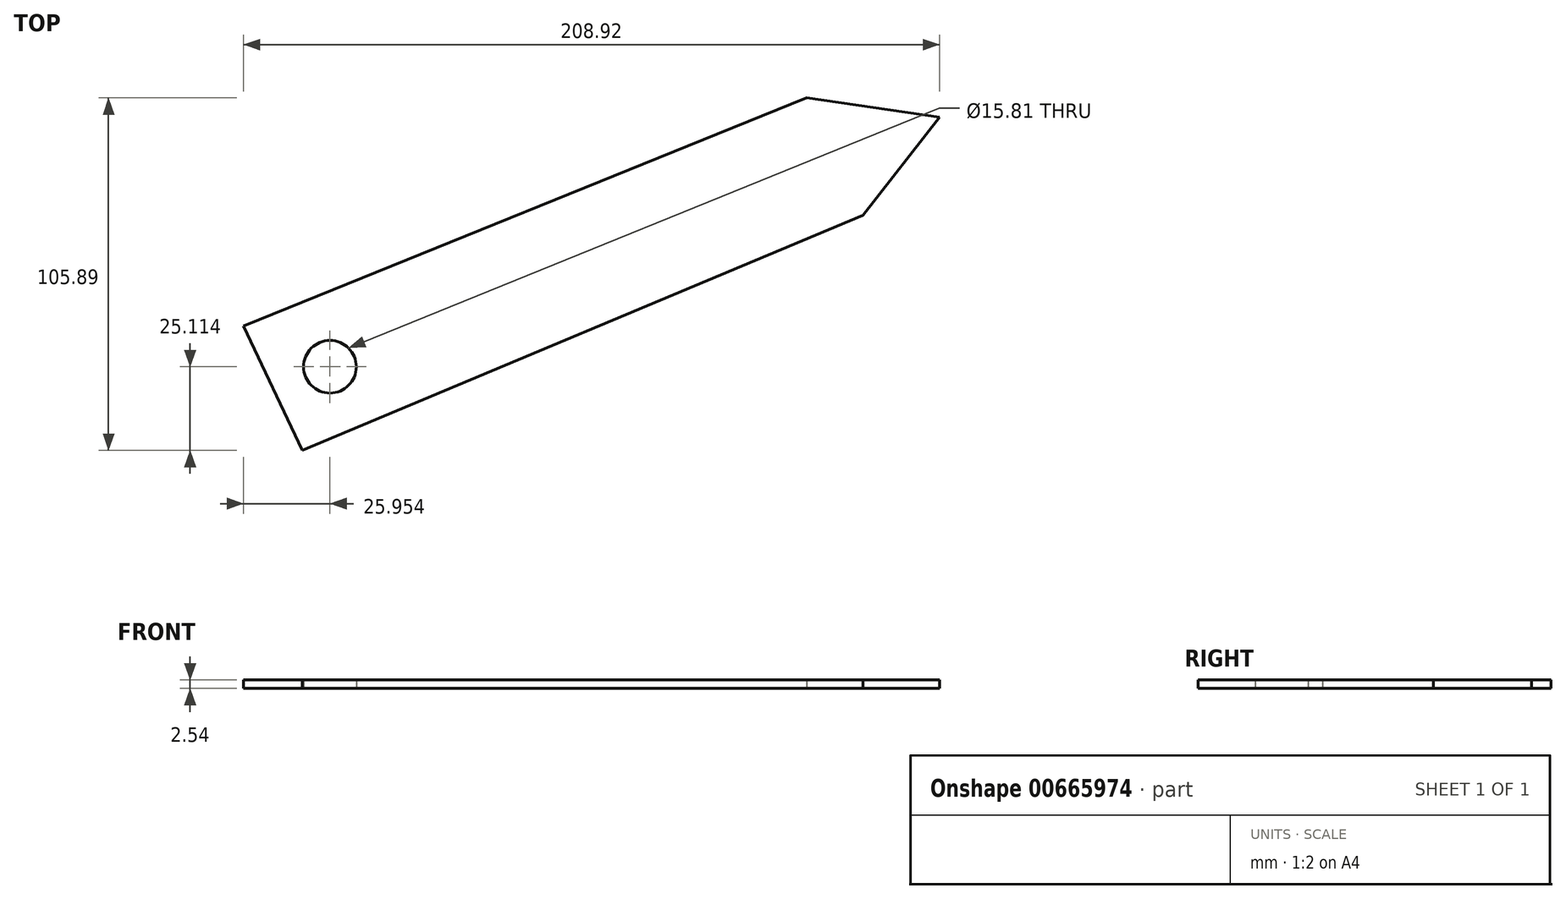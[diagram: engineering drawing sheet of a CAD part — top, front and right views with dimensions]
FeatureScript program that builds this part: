
annotation { "Feature Type Name" : "Feature", "Feature Type Description" : "" }
export const myFeature = defineFeature(function(context is Context, id is Id, definition is map)
    precondition{}
    {
        {
            var Q0;
            Q0=qCreatedBy(makeId("Top.planeOp"),FACE);
            var sketch = newSketch(context, id + "F0", { "sketchPlane" : qUnion([Q0])});
            skLineSegment(sketch, "E0", {"start": v(-77.2, -37.37) * mm, "end": v(91, 33.31) * mm});
            skLineSegment(sketch, "E1", {"start": v(91, 33.31) * mm, "end": v(114.05, 62.67) * mm});
            skLineSegment(sketch, "E2", {"start": v(114.05, 62.67) * mm, "end": v(74.17, 68.52) * mm});
            skLineSegment(sketch, "E3", {"start": v(74.17, 68.52) * mm, "end": v(-94.87, 0) * mm});
            skLineSegment(sketch, "E4", {"start": v(-94.87, 0) * mm, "end": v(-77.2, -37.37) * mm});
            skSolve(sketch);
        }
        {
            var Q0;
            Q0 = qSketchRegion(id + "F0", true);
            extrude(context, id + "F1", {"entities" : qUnion([Q0]), "depth" : 2.54 * mm, "offsetDistance" : 25.4 * mm});
        }
        {
            var Q0;
            Q0=makeQuery(id+"F1.opExtrude","CAP_FACE",FACE,{"disambiguationData":[OSD([sQuery(id+"F0.wireOp",EDGE,"E0"),sQuery(id+"F0.wireOp",EDGE,"E1"),sQuery(id+"F0.wireOp",EDGE,"E2"),sQuery(id+"F0.wireOp",EDGE,"E3"),sQuery(id+"F0.wireOp",EDGE,"E4")])],"isStart":true});
            var sketch = newSketch(context, id + "F2", { "sketchPlane" : qUnion([Q0])});
            skCircle(sketch, "E5", {"center": v(-68.92, 12.26) * mm, "radius": 7.9 * mm});
            skSolve(sketch);
        }
        {
            var Q0;
            Q0 = qSketchRegion(id + "F2", true);
            extrude(context, id + "F3", {"entities" : qUnion([Q0]), "operationType" : NewBodyOperationType.REMOVE, "oppositeDirection" : true, "depth" : 185.42 * mm, "offsetDistance" : 25.4 * mm});
        }
    });
